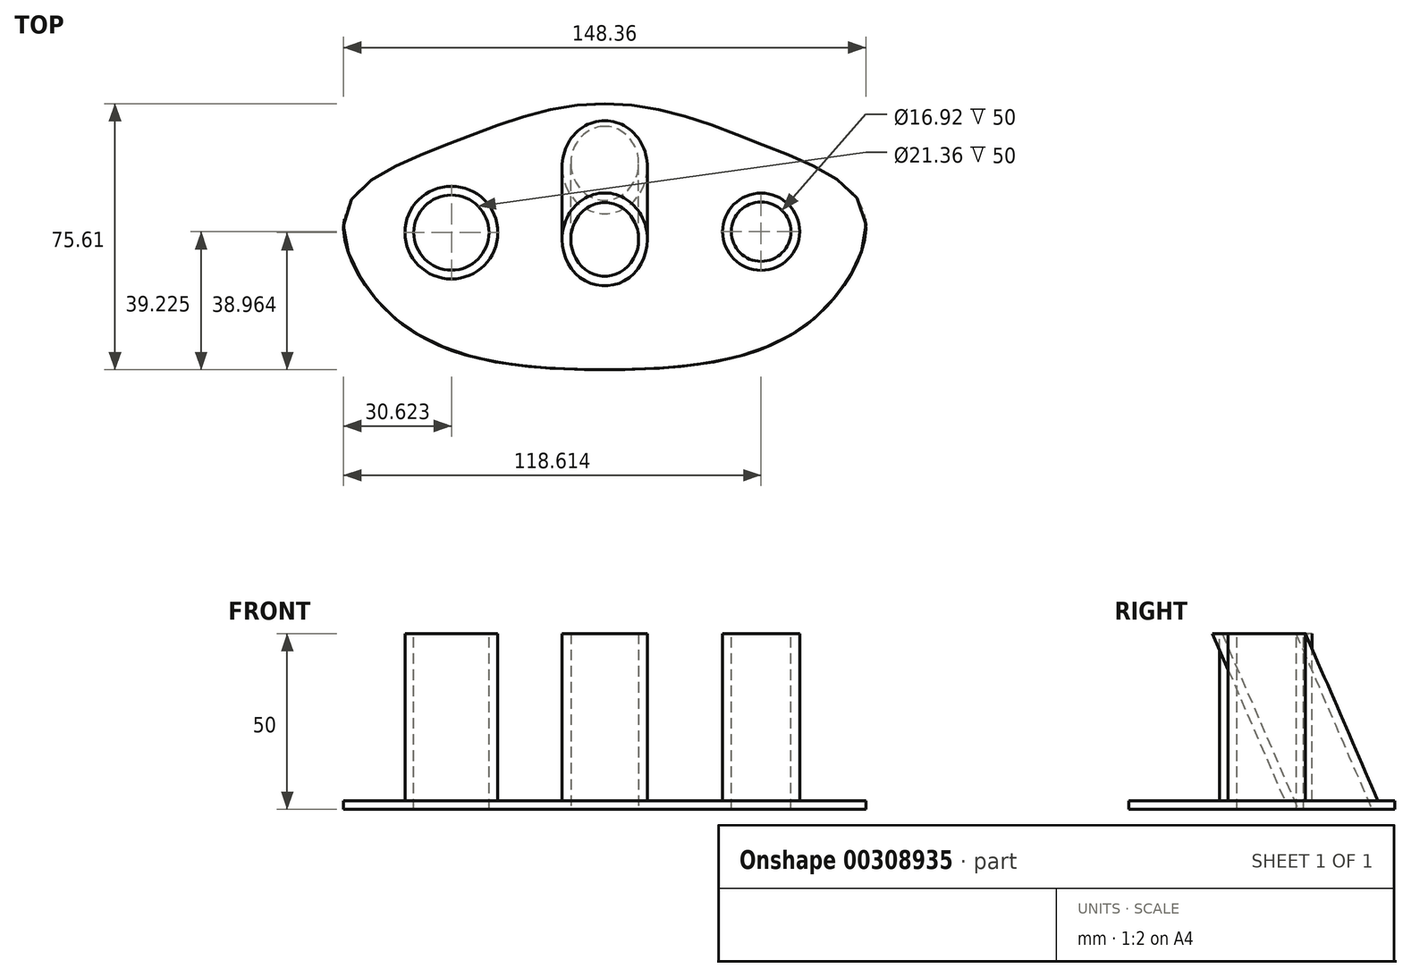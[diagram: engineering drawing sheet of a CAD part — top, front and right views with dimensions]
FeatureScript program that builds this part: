
annotation { "Feature Type Name" : "Feature", "Feature Type Description" : "" }
export const myFeature = defineFeature(function(context is Context, id is Id, definition is map)
    precondition{}
    {
        {
            var Q0;
            Q0=qCreatedBy(makeId("Top.planeOp"),FACE);
            var sketch = newSketch(context, id + "F0", { "sketchPlane" : qUnion([Q0])});
            skLineSegment(sketch, "E0", {"start": v(0, 0) * mm, "end": v(0, 75.61) * mm});
            skFitSpline(sketch, "E1", {"points": [v(0, 75.61) * mm, v(44.9, 63.91) * mm, v(73.5, 45.15) * mm, v(59.57, 14.63) * mm, v(0, 0) * mm], "startDerivative": vector(189.46, 0) * mm, "endDerivative": vector(-271.98, 0) * mm});
            skSolve(sketch);
        }
        {
            var Q0;
            Q0 = qSketchRegion(id + "F0", true);
            extrude(context, id + "F1", {"entities" : qUnion([Q0]), "depth" : 50 * mm});
        }
        {
            var Q0;
            Q0=makeQuery(id+"F1.opExtrude","SWEPT_BODY",BODY,{"disambiguationData":[OSD([sQuery(id+"F0.wireOp",EDGE,"E0"),sQuery(id+"F0.wireOp",EDGE,"E1")])]});
            var Q1;
            Q1=makeQuery(id+"F1.opExtrude","SWEPT_FACE",FACE,{"disambiguationData":[OSD([sQuery(id+"F0.wireOp",EDGE,"E0")])]});
            mirror(context, id + "F2", {"operationType" : NewBodyOperationType.ADD, "entities" : qUnion([Q0]), "mirrorPlane" : qUnion([Q1])});
        }
        {
            var Q0;
            Q0=qCreatedBy(makeId("Right.planeOp"),FACE);
            var sketch = newSketch(context, id + "F3", { "sketchPlane" : qUnion([Q0])});
            skLineSegment(sketch, "E2", {"start": v(30.9, 64.17) * mm, "end": v(62.57, -9.05) * mm});
            skLineSegment(sketch, "E3", {"start": v(62.57, -9.05) * mm, "end": v(71.41, -5.23) * mm});
            skLineSegment(sketch, "E4", {"start": v(71.41, -5.23) * mm, "end": v(41.05, 64.95) * mm});
            skLineSegment(sketch, "E5", {"start": v(41.05, 64.95) * mm, "end": v(30.9, 64.17) * mm});
            skSolve(sketch);
        }
        {
            var Q0;
            Q0 = qSketchRegion(id + "F3", true);
            var Q1;
            Q1=sQuery(id+"F3.wireOp",EDGE,"E2");
            revolve(context, id + "F4", {"operationType" : NewBodyOperationType.REMOVE, "entities" : qUnion([Q0]), "axis" : qUnion([Q1]), "revolveType" : RevolveType.FULL, "oppositeDirection" : true});
        }
        {
            var Q0;
            {var subQ0=makeQuery(id+"F1.opExtrude","CAP_FACE",FACE,{"disambiguationData":[OSD([sQuery(id+"F0.wireOp",EDGE,"E0"),sQuery(id+"F0.wireOp",EDGE,"E1")])],"isStart":false});Q0=makeQuery(id+"F2.boolean.opBoolean","MERGE",FACE,{"derivedFrom":[subQ0,makeQuery(id+"F2.opPattern","COPY",FACE,{"derivedFrom":subQ0,"instanceName":"1"})]});}
            var sketch = newSketch(context, id + "F5", { "sketchPlane" : qUnion([Q0])});
            skCircle(sketch, "E6", {"center": v(-43.56, 38.96) * mm, "radius": 10.68 * mm});
            skCircle(sketch, "E7", {"center": v(44.43, 39.22) * mm, "radius": 8.46 * mm});
            skSolve(sketch);
        }
        {
            var Q0;
            Q0 = qSketchRegion(id + "F5", true);
            extrude(context, id + "F6", {"entities" : qUnion([Q0]), "operationType" : NewBodyOperationType.REMOVE, "endBound" : BoundingType.THROUGH_ALL, "oppositeDirection" : true, "depth" : 25 * mm});
        }
        {
            var Q0;
            {var subQ0=makeQuery(id+"F1.opExtrude","CAP_FACE",FACE,{"disambiguationData":[OSD([sQuery(id+"F0.wireOp",EDGE,"E0"),sQuery(id+"F0.wireOp",EDGE,"E1")])],"isStart":false});Q0=makeQuery(id+"F2.boolean.opBoolean","MERGE",FACE,{"derivedFrom":[subQ0,makeQuery(id+"F2.opPattern","COPY",FACE,{"derivedFrom":subQ0,"instanceName":"1"})]});}
            var Q1;
            Q1=makeQuery(id+"F2.opPattern","COPY",FACE,{"derivedFrom":makeQuery(id+"F1.opExtrude","SWEPT_FACE",FACE,{"disambiguationData":[OSD([sQuery(id+"F0.wireOp",EDGE,"E1")])]}),"instanceName":"1"});
            var Q2;
            Q2=makeQuery(id+"F1.opExtrude","SWEPT_FACE",FACE,{"disambiguationData":[OSD([sQuery(id+"F0.wireOp",EDGE,"E1")])]});
            shell(context, id + "F7", {"entities" : qUnion([Q0, Q1, Q2]), "thickness" : 2.5 * mm});
        }
    });
